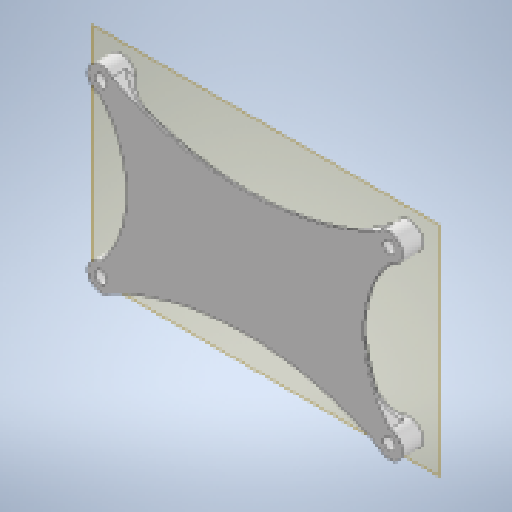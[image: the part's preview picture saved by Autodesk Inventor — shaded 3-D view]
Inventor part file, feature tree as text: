
AUTODESK INVENTOR PART (.ipt)
format: ipt  version: 2024.1 (Build 281209000, 209)  size: 370,176 bytes
history: native  units: mm
features: reference x4, projected_geometry x3, extrude x2, sketch x2, other x2, plane x1, fillet x1, chamfer x1
ambient origin geometry x8: Origin, YZ Plane, XZ Plane, XY Plane, X Axis, Y Axis, Z Axis, Center Point
bodies: Solid1 (feature_tree)
feature tree (16):
  plane  "Work Plane1"
  extrude  "Extrusion1"  Depth=2.0mm
  extrude  "Extrusion2"  Depth=30.0mm
  fillet  "Fillet1"  Radius=80.0mm
  chamfer  "Chamfer1"  Distance=2.0mm
  sketch  "Sketch1"  dims[d0=2.0mm d1=2.0mm]
  reference  "Reference1"
  reference  "Reference2"
  reference  "Reference3"
  sketch  "Sketch2"  dims[d2=3.5mm d3=0.0mm d4=30.0mm d5=80.0mm d6=2.0mm d7=0.0mm d8=10.0mm d9=1.5mm d10=2.0mm d11=45.0deg]
  reference  "Reference4"
  projected_geometry  "Projected Loop1"
  projected_geometry  "Projected Loop2"
  projected_geometry  "Projected Loop3"
  other  "Assembly1"
  other  "diode-ladder-filter-synth-module:1"
